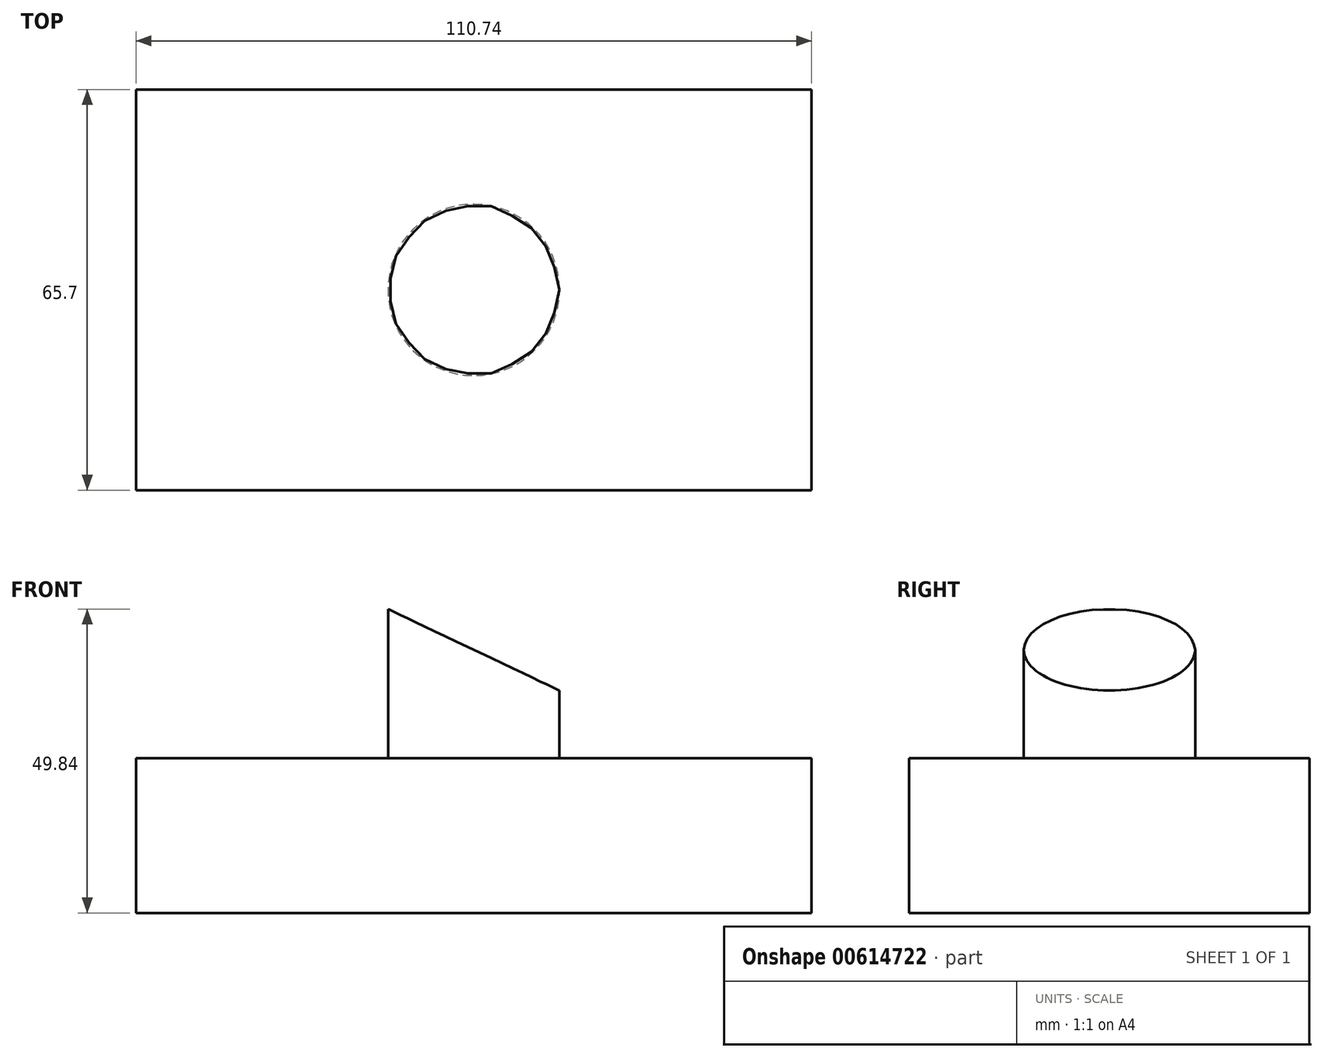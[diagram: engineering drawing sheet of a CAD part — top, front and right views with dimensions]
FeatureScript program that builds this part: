
annotation { "Feature Type Name" : "Feature", "Feature Type Description" : "" }
export const myFeature = defineFeature(function(context is Context, id is Id, definition is map)
    precondition{}
    {
        {
            var Q0;
            Q0=qCreatedBy(makeId("Top.planeOp"),FACE);
            var sketch = newSketch(context, id + "F0", { "sketchPlane" : qUnion([Q0])});
            skLineSegment(sketch, "E0.bottom", {"start": v(-55.37, 32.85) * mm, "end": v(55.37, 32.85) * mm});
            skLineSegment(sketch, "E0.top", {"start": v(-55.37, -32.85) * mm, "end": v(55.37, -32.85) * mm});
            skLineSegment(sketch, "E0.left", {"start": v(-55.37, 32.85) * mm, "end": v(-55.37, -32.85) * mm});
            skLineSegment(sketch, "E0.right", {"start": v(55.37, 32.85) * mm, "end": v(55.37, -32.85) * mm});
            skPoint(sketch, "E0.middle", {"position": v(0, 0) * mm});
            skSolve(sketch);
        }
        {
            var Q0;
            Q0 = qSketchRegion(id + "F0", true);
            extrude(context, id + "F1", {"entities" : qUnion([Q0]), "depth" : 25.4 * mm, "offsetDistance" : 25.4 * mm});
        }
        {
            var Q0;
            Q0=makeQuery(id+"F1.opExtrude","CAP_FACE",FACE,{"disambiguationData":[OSD([sQuery(id+"F0.wireOp",EDGE,"E0.bottom"),sQuery(id+"F0.wireOp",EDGE,"E0.top"),sQuery(id+"F0.wireOp",EDGE,"E0.left"),sQuery(id+"F0.wireOp",EDGE,"E0.right")])],"isStart":false});
            var sketch = newSketch(context, id + "F2", { "sketchPlane" : qUnion([Q0])});
            skCircle(sketch, "E1", {"center": v(0, 0) * mm, "radius": 14.06 * mm});
            skSolve(sketch);
        }
        {
            var Q0;
            Q0 = qSketchRegion(id + "F2", true);
            extrude(context, id + "F3", {"entities" : qUnion([Q0]), "operationType" : NewBodyOperationType.ADD, "depth" : 50.8 * mm, "offsetDistance" : 25.4 * mm});
        }
        {
            var Q0;
            Q0=qCreatedBy(makeId("Front.planeOp"),FACE);
            var sketch = newSketch(context, id + "F4", { "sketchPlane" : qUnion([Q0])});
            skLineSegment(sketch, "E2", {"start": v(-22.95, 54.07) * mm, "end": v(27.75, 54.07) * mm});
            skLineSegment(sketch, "E3", {"start": v(27.75, 54.07) * mm, "end": v(27.75, 29.96) * mm});
            skLineSegment(sketch, "E4", {"start": v(-22.95, 54.07) * mm, "end": v(27.75, 29.96) * mm});
            skSolve(sketch);
        }
        {
            var Q0;
            Q0 = qSketchRegion(id + "F4", true);
            extrude(context, id + "F5", {"entities" : qUnion([Q0]), "operationType" : NewBodyOperationType.REMOVE, "endBound" : BoundingType.SYMMETRIC, "oppositeDirection" : true, "depth" : 101.6 * mm, "offsetDistance" : 25.4 * mm});
        }
        {
            var Q0;
            Q0=qCreatedBy(makeId("Front.planeOp"),FACE);
            var sketch = newSketch(context, id + "F6", { "sketchPlane" : qUnion([Q0])});
            skLineSegment(sketch, "E5", {"start": v(-32.98, 52.9) * mm, "end": v(34.76, 52.9) * mm});
            skLineSegment(sketch, "E6", {"start": v(-32.98, 52.9) * mm, "end": v(-32.98, 81.52) * mm});
            skLineSegment(sketch, "E7", {"start": v(-32.98, 81.52) * mm, "end": v(27.65, 81.52) * mm});
            skLineSegment(sketch, "E8", {"start": v(27.65, 81.52) * mm, "end": v(34.76, 52.9) * mm});
            skSolve(sketch);
        }
        {
            var Q0;
            Q0 = qSketchRegion(id + "F6", true);
            extrude(context, id + "F7", {"entities" : qUnion([Q0]), "operationType" : NewBodyOperationType.REMOVE, "endBound" : BoundingType.SYMMETRIC, "depth" : 50.8 * mm, "offsetDistance" : 25.4 * mm});
        }
    });
